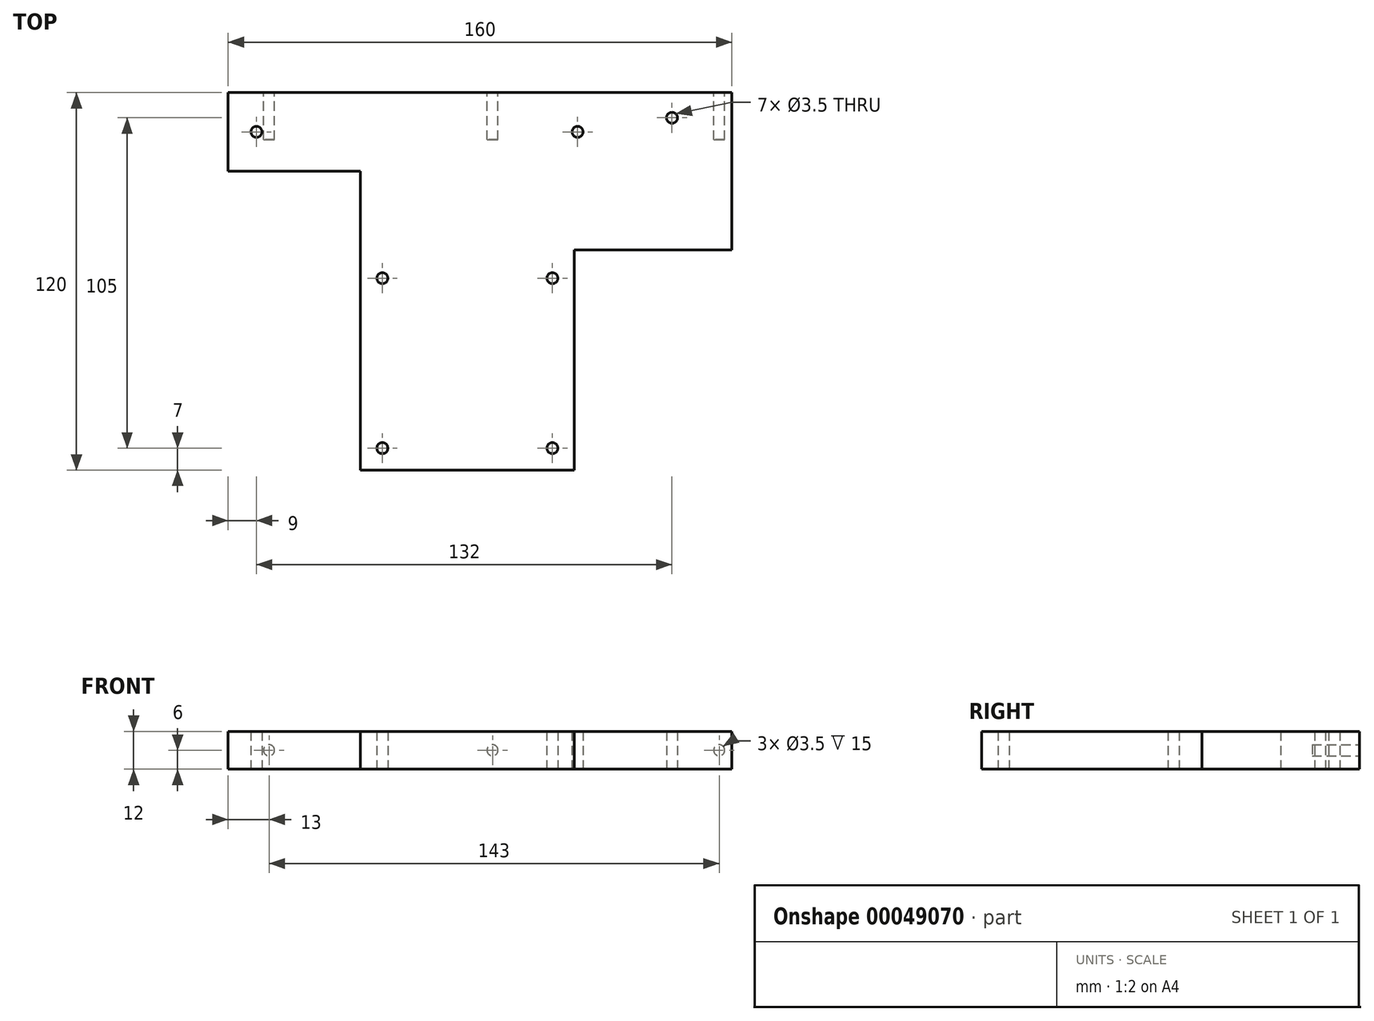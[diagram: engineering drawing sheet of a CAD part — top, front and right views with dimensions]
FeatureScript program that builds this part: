
annotation { "Feature Type Name" : "Feature", "Feature Type Description" : "" }
export const myFeature = defineFeature(function(context is Context, id is Id, definition is map)
    precondition{}
    {
        {
            var Q0;
            Q0=qCreatedBy(makeId("Top.planeOp"),FACE);
            var sketch = newSketch(context, id + "F0", { "sketchPlane" : qUnion([Q0])});
            skLineSegment(sketch, "E0", {"start": v(0, 0) * mm, "end": v(160, 0) * mm});
            skLineSegment(sketch, "E1", {"start": v(160, 0) * mm, "end": v(160, -50) * mm});
            skLineSegment(sketch, "E2", {"start": v(160, -50) * mm, "end": v(110, -50) * mm});
            skLineSegment(sketch, "E3", {"start": v(110, -50) * mm, "end": v(110, -120) * mm});
            skLineSegment(sketch, "E4", {"start": v(110, -120) * mm, "end": v(42, -120) * mm});
            skLineSegment(sketch, "E5", {"start": v(42, -120) * mm, "end": v(42, -25) * mm});
            skLineSegment(sketch, "E6", {"start": v(42, -25) * mm, "end": v(0, -25) * mm});
            skLineSegment(sketch, "E7", {"start": v(0, -25) * mm, "end": v(0, 0) * mm});
            skCircle(sketch, "E8", {"center": v(9, -12.5) * mm, "radius": 1.75 * mm});
            skPoint(sketch, "E8.centerSnap0", {"position": v(0, -12.5) * mm});
            skCircle(sketch, "E9", {"center": v(111, -12.5) * mm, "radius": 1.75 * mm});
            skCircle(sketch, "E10", {"center": v(141, -8) * mm, "radius": 1.75 * mm});
            skCircle(sketch, "E11", {"center": v(49, -59) * mm, "radius": 1.75 * mm});
            skCircle(sketch, "E12", {"center": v(103, -59) * mm, "radius": 1.75 * mm});
            skCircle(sketch, "E13", {"center": v(49, -113) * mm, "radius": 1.75 * mm});
            skCircle(sketch, "E14", {"center": v(103, -113) * mm, "radius": 1.75 * mm});
            skLineSegment(sketch, "E15", {"start": v(49, -113) * mm, "end": v(103, -113) * mm, "construction": true});
            skLineSegment(sketch, "E16", {"start": v(76, -120) * mm, "end": v(76, -113) * mm, "construction": true});
            skSolve(sketch);
        }
        {
            var Q0;
            Q0 = qSketchRegion(id + "F0", true);
            extrude(context, id + "F1", {"entities" : qUnion([Q0]), "depth" : 12 * mm});
        }
        {
            var Q0;
            Q0=makeQuery(id+"F1.opExtrude","SWEPT_FACE",FACE,{"disambiguationData":[OSD([sQuery(id+"F0.wireOp",EDGE,"E0")])]});
            var sketch = newSketch(context, id + "F2", { "sketchPlane" : qUnion([Q0])});
            skCircle(sketch, "E17", {"center": v(-156, 6) * mm, "radius": 1.75 * mm});
            skCircle(sketch, "E18", {"center": v(-84, 6) * mm, "radius": 1.75 * mm});
            skCircle(sketch, "E19", {"center": v(-13, 6) * mm, "radius": 1.75 * mm});
            skSolve(sketch);
        }
        {
            var Q0;
            Q0 = qSketchRegion(id + "F2", true);
            extrude(context, id + "F3", {"entities" : qUnion([Q0]), "operationType" : NewBodyOperationType.REMOVE, "oppositeDirection" : true, "depth" : 15 * mm});
        }
    });
